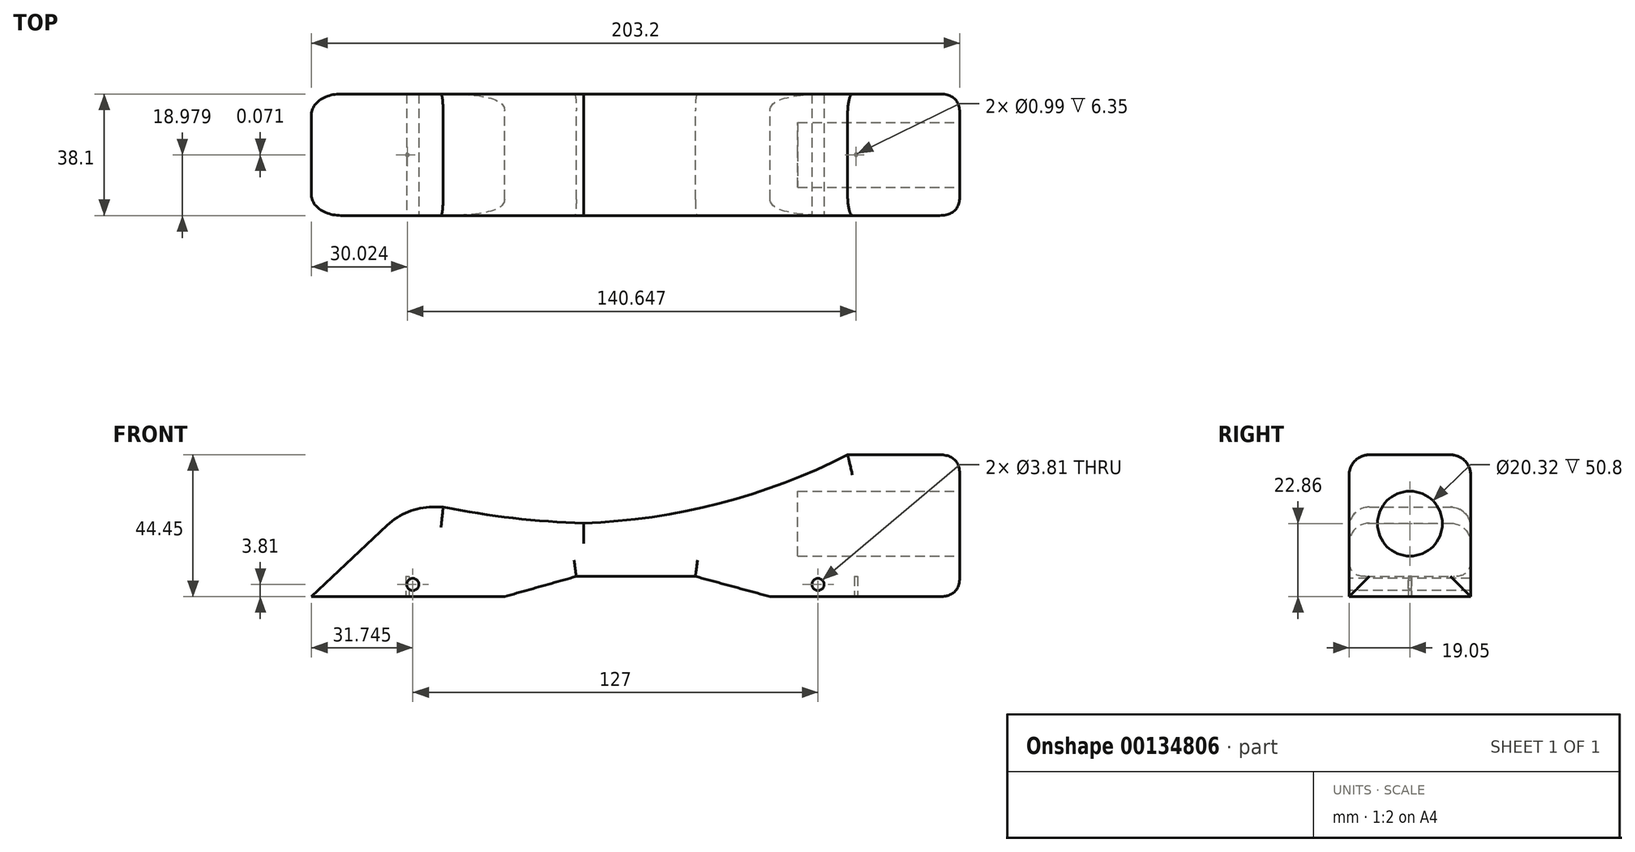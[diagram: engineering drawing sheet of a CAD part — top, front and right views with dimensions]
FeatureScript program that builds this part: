
annotation { "Feature Type Name" : "Feature", "Feature Type Description" : "" }
export const myFeature = defineFeature(function(context is Context, id is Id, definition is map)
    precondition{}
    {
        {
            var Q0;
            Q0=qCreatedBy(makeId("Front.planeOp"),FACE);
            var sketch = newSketch(context, id + "F0", { "sketchPlane" : qUnion([Q0])});
            skLineSegment(sketch, "E0", {"start": v(-93.71, 0) * mm, "end": v(-64, 28.05) * mm});
            skLineSegment(sketch, "E1", {"start": v(-64, 28.05) * mm, "end": v(-52.47, 28.05) * mm});
            skLineSegment(sketch, "E2", {"start": v(-52.47, 28.05) * mm, "end": v(-40.94, 22.9) * mm});
            skLineSegment(sketch, "E3", {"start": v(-40.94, 22.9) * mm, "end": v(49.74, 22.9) * mm});
            skLineSegment(sketch, "E4", {"start": v(49.74, 22.9) * mm, "end": v(74.3, 44.45) * mm});
            skLineSegment(sketch, "E5", {"start": v(74.3, 44.45) * mm, "end": v(109.49, 44.45) * mm});
            skLineSegment(sketch, "E6", {"start": v(109.49, 44.45) * mm, "end": v(109.49, 0) * mm});
            skLineSegment(sketch, "E7", {"start": v(109.49, 0) * mm, "end": v(-93.71, 0) * mm});
            skLineSegment(sketch, "E8", {"start": v(-33.22, 0) * mm, "end": v(-10.73, 6.32) * mm});
            skLineSegment(sketch, "E9", {"start": v(-10.73, 6.32) * mm, "end": v(26.6, 6.32) * mm});
            skLineSegment(sketch, "E10", {"start": v(26.6, 6.32) * mm, "end": v(50.03, 0) * mm});
            skSolve(sketch);
        }
        {
            var Q0;
            Q0=makeQuery(id+"F0.imprint","IMPRINT",FACE,{"disambiguationData":[TD([[makeQuery(id+"F0.imprint","IMPRINT",EDGE,{"derivedFrom":sQuery(id+"F0.wireOp",EDGE,"E0")}),-1.0]])]});
            extrude(context, id + "F1", {"entities" : qUnion([Q0]), "depth" : 38.1 * mm});
        }
        {
            var Q0;
            Q0=makeQuery(id+"F1.opExtrude","SWEPT_EDGE",EDGE,{"disambiguationData":[OSD([sQuery(id+"F0.wireOp",EDGE,"E0"),sQuery(id+"F0.wireOp",EDGE,"E1")])]});
            fillet(context, id + "F2", {"entities" : qUnion([Q0]), "radius" : 20.77 * mm, "tangentPropagation" : true, "allowEdgeOverflow" : false});
        }
        {
            var Q0;
            Q0=makeQuery(id+"F1.opExtrude","SWEPT_EDGE",EDGE,{"disambiguationData":[OSD([sQuery(id+"F0.wireOp",EDGE,"E3"),sQuery(id+"F0.wireOp",EDGE,"E4")])]});
            fillet(context, id + "F3", {"entities" : qUnion([Q0]), "radius" : 197.48 * mm, "tangentPropagation" : true, "allowEdgeOverflow" : false});
        }
        {
            var Q0;
            Q0=makeQuery(id+"F1.opExtrude","SWEPT_EDGE",EDGE,{"disambiguationData":[OSD([sQuery(id+"F0.wireOp",EDGE,"E2"),sQuery(id+"F0.wireOp",EDGE,"E3")])]});
            fillet(context, id + "F4", {"entities" : qUnion([Q0]), "radius" : 266.42 * mm, "tangentPropagation" : true, "allowEdgeOverflow" : false});
        }
        {
            var Q0;
            Q0=makeQuery(id+"F1.opExtrude","CAP_EDGE",EDGE,{"disambiguationData":[OSD([sQuery(id+"F0.wireOp",EDGE,"E0")])],"isStart":false});
            var Q1;
            {var subQ0=sQuery(id+"F0.wireOp",EDGE,"E1");var subQ1=sQuery(id+"F0.wireOp",EDGE,"E0");Q1=makeQuery(id+"F2.opFillet","BLEND_EDGE",EDGE,{"blendedFrom":[makeQuery(id+"F1.opExtrude","SWEPT_EDGE",EDGE,{"disambiguationData":[OSD([subQ1,subQ0])]}),makeQuery(id+"F1.opExtrude","CAP_FACE",FACE,{"disambiguationData":[OSD([subQ1,subQ0,sQuery(id+"F0.wireOp",EDGE,"E2"),sQuery(id+"F0.wireOp",EDGE,"E3"),sQuery(id+"F0.wireOp",EDGE,"E4"),sQuery(id+"F0.wireOp",EDGE,"E5"),sQuery(id+"F0.wireOp",EDGE,"E6"),sQuery(id+"F0.wireOp",EDGE,"E7")])],"isStart":false})],"blendedInto":[makeQuery(id+"F1.opExtrude","CAP_FACE",FACE,{"disambiguationData":[OSD([subQ1,subQ0,sQuery(id+"F0.wireOp",EDGE,"E2"),sQuery(id+"F0.wireOp",EDGE,"E3"),sQuery(id+"F0.wireOp",EDGE,"E4"),sQuery(id+"F0.wireOp",EDGE,"E5"),sQuery(id+"F0.wireOp",EDGE,"E6"),sQuery(id+"F0.wireOp",EDGE,"E7")])],"isStart":false})]});}
            var Q2;
            {var subQ0=sQuery(id+"F0.wireOp",EDGE,"E3");var subQ1=sQuery(id+"F0.wireOp",EDGE,"E2");Q2=makeQuery(id+"F4.opFillet","BLEND_EDGE",EDGE,{"blendedFrom":[makeQuery(id+"F1.opExtrude","SWEPT_EDGE",EDGE,{"disambiguationData":[OSD([subQ1,subQ0])]}),makeQuery(id+"F1.opExtrude","CAP_FACE",FACE,{"disambiguationData":[OSD([sQuery(id+"F0.wireOp",EDGE,"E0"),sQuery(id+"F0.wireOp",EDGE,"E1"),subQ1,subQ0,sQuery(id+"F0.wireOp",EDGE,"E4"),sQuery(id+"F0.wireOp",EDGE,"E5"),sQuery(id+"F0.wireOp",EDGE,"E6"),sQuery(id+"F0.wireOp",EDGE,"E7")])],"isStart":false})],"blendedInto":[makeQuery(id+"F1.opExtrude","CAP_FACE",FACE,{"disambiguationData":[OSD([sQuery(id+"F0.wireOp",EDGE,"E0"),sQuery(id+"F0.wireOp",EDGE,"E1"),subQ1,subQ0,sQuery(id+"F0.wireOp",EDGE,"E4"),sQuery(id+"F0.wireOp",EDGE,"E5"),sQuery(id+"F0.wireOp",EDGE,"E6"),sQuery(id+"F0.wireOp",EDGE,"E7")])],"isStart":false})]});}
            var Q3;
            {var subQ0=sQuery(id+"F0.wireOp",EDGE,"E4");var subQ1=sQuery(id+"F0.wireOp",EDGE,"E3");Q3=makeQuery(id+"F3.opFillet","BLEND_EDGE",EDGE,{"blendedFrom":[makeQuery(id+"F1.opExtrude","SWEPT_EDGE",EDGE,{"disambiguationData":[OSD([subQ1,subQ0])]}),makeQuery(id+"F1.opExtrude","CAP_FACE",FACE,{"disambiguationData":[OSD([sQuery(id+"F0.wireOp",EDGE,"E0"),sQuery(id+"F0.wireOp",EDGE,"E1"),sQuery(id+"F0.wireOp",EDGE,"E2"),subQ1,subQ0,sQuery(id+"F0.wireOp",EDGE,"E5"),sQuery(id+"F0.wireOp",EDGE,"E6"),sQuery(id+"F0.wireOp",EDGE,"E7")])],"isStart":false})],"blendedInto":[makeQuery(id+"F1.opExtrude","CAP_FACE",FACE,{"disambiguationData":[OSD([sQuery(id+"F0.wireOp",EDGE,"E0"),sQuery(id+"F0.wireOp",EDGE,"E1"),sQuery(id+"F0.wireOp",EDGE,"E2"),subQ1,subQ0,sQuery(id+"F0.wireOp",EDGE,"E5"),sQuery(id+"F0.wireOp",EDGE,"E6"),sQuery(id+"F0.wireOp",EDGE,"E7")])],"isStart":false})]});}
            var Q4;
            Q4=makeQuery(id+"F1.opExtrude","CAP_EDGE",EDGE,{"disambiguationData":[OSD([sQuery(id+"F0.wireOp",EDGE,"E5")])],"isStart":false});
            fillet(context, id + "F5", {"entities" : qUnion([Q0, Q1, Q2, Q3, Q4]), "radius" : 6.35 * mm, "tangentPropagation" : true, "allowEdgeOverflow" : false});
        }
        {
            var Q0;
            Q0=makeQuery(id+"F1.opExtrude","CAP_EDGE",EDGE,{"disambiguationData":[OSD([sQuery(id+"F0.wireOp",EDGE,"E0")])],"isStart":true});
            var Q1;
            {var subQ0=sQuery(id+"F0.wireOp",EDGE,"E1");var subQ1=sQuery(id+"F0.wireOp",EDGE,"E0");Q1=makeQuery(id+"F2.opFillet","BLEND_EDGE",EDGE,{"blendedFrom":[makeQuery(id+"F1.opExtrude","SWEPT_EDGE",EDGE,{"disambiguationData":[OSD([subQ1,subQ0])]}),makeQuery(id+"F1.opExtrude","CAP_FACE",FACE,{"disambiguationData":[OSD([subQ1,subQ0,sQuery(id+"F0.wireOp",EDGE,"E2"),sQuery(id+"F0.wireOp",EDGE,"E3"),sQuery(id+"F0.wireOp",EDGE,"E4"),sQuery(id+"F0.wireOp",EDGE,"E5"),sQuery(id+"F0.wireOp",EDGE,"E6"),sQuery(id+"F0.wireOp",EDGE,"E7")])],"isStart":true})],"blendedInto":[makeQuery(id+"F1.opExtrude","CAP_FACE",FACE,{"disambiguationData":[OSD([subQ1,subQ0,sQuery(id+"F0.wireOp",EDGE,"E2"),sQuery(id+"F0.wireOp",EDGE,"E3"),sQuery(id+"F0.wireOp",EDGE,"E4"),sQuery(id+"F0.wireOp",EDGE,"E5"),sQuery(id+"F0.wireOp",EDGE,"E6"),sQuery(id+"F0.wireOp",EDGE,"E7")])],"isStart":true})]});}
            var Q2;
            {var subQ0=sQuery(id+"F0.wireOp",EDGE,"E3");var subQ1=sQuery(id+"F0.wireOp",EDGE,"E2");Q2=makeQuery(id+"F4.opFillet","BLEND_EDGE",EDGE,{"blendedFrom":[makeQuery(id+"F1.opExtrude","SWEPT_EDGE",EDGE,{"disambiguationData":[OSD([subQ1,subQ0])]}),makeQuery(id+"F1.opExtrude","CAP_FACE",FACE,{"disambiguationData":[OSD([sQuery(id+"F0.wireOp",EDGE,"E0"),sQuery(id+"F0.wireOp",EDGE,"E1"),subQ1,subQ0,sQuery(id+"F0.wireOp",EDGE,"E4"),sQuery(id+"F0.wireOp",EDGE,"E5"),sQuery(id+"F0.wireOp",EDGE,"E6"),sQuery(id+"F0.wireOp",EDGE,"E7")])],"isStart":true})],"blendedInto":[makeQuery(id+"F1.opExtrude","CAP_FACE",FACE,{"disambiguationData":[OSD([sQuery(id+"F0.wireOp",EDGE,"E0"),sQuery(id+"F0.wireOp",EDGE,"E1"),subQ1,subQ0,sQuery(id+"F0.wireOp",EDGE,"E4"),sQuery(id+"F0.wireOp",EDGE,"E5"),sQuery(id+"F0.wireOp",EDGE,"E6"),sQuery(id+"F0.wireOp",EDGE,"E7")])],"isStart":true})]});}
            var Q3;
            {var subQ0=sQuery(id+"F0.wireOp",EDGE,"E4");var subQ1=sQuery(id+"F0.wireOp",EDGE,"E3");Q3=makeQuery(id+"F3.opFillet","BLEND_EDGE",EDGE,{"blendedFrom":[makeQuery(id+"F1.opExtrude","SWEPT_EDGE",EDGE,{"disambiguationData":[OSD([subQ1,subQ0])]}),makeQuery(id+"F1.opExtrude","CAP_FACE",FACE,{"disambiguationData":[OSD([sQuery(id+"F0.wireOp",EDGE,"E0"),sQuery(id+"F0.wireOp",EDGE,"E1"),sQuery(id+"F0.wireOp",EDGE,"E2"),subQ1,subQ0,sQuery(id+"F0.wireOp",EDGE,"E5"),sQuery(id+"F0.wireOp",EDGE,"E6"),sQuery(id+"F0.wireOp",EDGE,"E7")])],"isStart":true})],"blendedInto":[makeQuery(id+"F1.opExtrude","CAP_FACE",FACE,{"disambiguationData":[OSD([sQuery(id+"F0.wireOp",EDGE,"E0"),sQuery(id+"F0.wireOp",EDGE,"E1"),sQuery(id+"F0.wireOp",EDGE,"E2"),subQ1,subQ0,sQuery(id+"F0.wireOp",EDGE,"E5"),sQuery(id+"F0.wireOp",EDGE,"E6"),sQuery(id+"F0.wireOp",EDGE,"E7")])],"isStart":true})]});}
            var Q4;
            Q4=makeQuery(id+"F1.opExtrude","CAP_EDGE",EDGE,{"disambiguationData":[OSD([sQuery(id+"F0.wireOp",EDGE,"E5")])],"isStart":true});
            fillet(context, id + "F6", {"entities" : qUnion([Q0, Q1, Q2, Q3, Q4]), "radius" : 6.35 * mm, "tangentPropagation" : true, "allowEdgeOverflow" : false});
        }
        {
            var Q0;
            Q0=makeQuery(id+"F1.opExtrude","CAP_FACE",FACE,{"disambiguationData":[OSD([sQuery(id+"F0.wireOp",EDGE,"E0"),sQuery(id+"F0.wireOp",EDGE,"E1"),sQuery(id+"F0.wireOp",EDGE,"E2"),sQuery(id+"F0.wireOp",EDGE,"E3"),sQuery(id+"F0.wireOp",EDGE,"E4"),sQuery(id+"F0.wireOp",EDGE,"E5"),sQuery(id+"F0.wireOp",EDGE,"E6"),sQuery(id+"F0.wireOp",EDGE,"E7"),sQuery(id+"F0.wireOp",EDGE,"E8"),sQuery(id+"F0.wireOp",EDGE,"E9"),sQuery(id+"F0.wireOp",EDGE,"E10")])],"isStart":false});
            var sketch = newSketch(context, id + "F7", { "sketchPlane" : qUnion([Q0])});
            skCircle(sketch, "E11", {"center": v(-61.96, 3.81) * mm, "radius": 1.9 * mm});
            skSolve(sketch);
        }
        {
            var Q0;
            Q0=makeQuery(id+"F7.imprint","IMPRINT",FACE,{"disambiguationData":[TD([[makeQuery(id+"F7.imprint","IMPRINT",EDGE,{"derivedFrom":sQuery(id+"F7.wireOp",EDGE,"E11")}),1.0]])]});
            extrude(context, id + "F8", {"entities" : qUnion([Q0]), "operationType" : NewBodyOperationType.REMOVE, "endBound" : BoundingType.THROUGH_ALL, "oppositeDirection" : true, "depth" : 25.4 * mm});
        }
        {
            var Q0;
            Q0=makeQuery(id+"F1.opExtrude","CAP_FACE",FACE,{"disambiguationData":[OSD([sQuery(id+"F0.wireOp",EDGE,"E0"),sQuery(id+"F0.wireOp",EDGE,"E1"),sQuery(id+"F0.wireOp",EDGE,"E2"),sQuery(id+"F0.wireOp",EDGE,"E3"),sQuery(id+"F0.wireOp",EDGE,"E4"),sQuery(id+"F0.wireOp",EDGE,"E5"),sQuery(id+"F0.wireOp",EDGE,"E6"),sQuery(id+"F0.wireOp",EDGE,"E7"),sQuery(id+"F0.wireOp",EDGE,"E8"),sQuery(id+"F0.wireOp",EDGE,"E9"),sQuery(id+"F0.wireOp",EDGE,"E10")])],"isStart":false});
            var sketch = newSketch(context, id + "F9", { "sketchPlane" : qUnion([Q0])});
            skCircle(sketch, "E12", {"center": v(65.04, 3.81) * mm, "radius": 1.9 * mm});
            skSolve(sketch);
        }
        {
            var Q0;
            Q0=makeQuery(id+"F9.imprint","IMPRINT",FACE,{"disambiguationData":[TD([[makeQuery(id+"F9.imprint","IMPRINT",EDGE,{"derivedFrom":sQuery(id+"F9.wireOp",EDGE,"E12")}),1.0]])]});
            var Q1;
            Q1=sQuery(id+"F9.wireOp",EDGE,"E12");
            extrude(context, id + "F10", {"entities" : qUnion([Q0]), "operationType" : NewBodyOperationType.REMOVE, "surfaceEntities" : qUnion([Q1]), "endBound" : BoundingType.THROUGH_ALL, "oppositeDirection" : true, "depth" : 25.4 * mm});
        }
        {
            var Q0;
            Q0=makeQuery(id+"F1.opExtrude","SWEPT_FACE",FACE,{"disambiguationData":[OSD([sQuery(id+"F0.wireOp",EDGE,"E6")])]});
            var sketch = newSketch(context, id + "F11", { "sketchPlane" : qUnion([Q0])});
            skCircle(sketch, "E13", {"center": v(-19.05, 22.86) * mm, "radius": 10.16 * mm});
            skSolve(sketch);
        }
        {
            var Q0;
            Q0=makeQuery(id+"F11.imprint","IMPRINT",FACE,{"disambiguationData":[TD([[makeQuery(id+"F11.imprint","IMPRINT",EDGE,{"derivedFrom":sQuery(id+"F11.wireOp",EDGE,"E13")}),1.0]])]});
            var Q1;
            Q1=sQuery(id+"F11.wireOp",EDGE,"E13");
            extrude(context, id + "F12", {"entities" : qUnion([Q0]), "operationType" : NewBodyOperationType.REMOVE, "surfaceEntities" : qUnion([Q1]), "oppositeDirection" : true, "depth" : 50.8 * mm});
        }
        {
            var Q0;
            Q0=makeQuery(id+"F1.opExtrude","CAP_EDGE",EDGE,{"disambiguationData":[OSD([sQuery(id+"F0.wireOp",EDGE,"E8")])],"isStart":false});
            var Q1;
            Q1=makeQuery(id+"F1.opExtrude","CAP_EDGE",EDGE,{"disambiguationData":[OSD([sQuery(id+"F0.wireOp",EDGE,"E9")])],"isStart":false});
            var Q2;
            Q2=makeQuery(id+"F1.opExtrude","CAP_EDGE",EDGE,{"disambiguationData":[OSD([sQuery(id+"F0.wireOp",EDGE,"E10")])],"isStart":false});
            fillet(context, id + "F13", {"entities" : qUnion([Q0, Q1, Q2]), "radius" : 5.08 * mm, "tangentPropagation" : true, "rho" : 0.5, "crossSection" : FilletCrossSection.CONIC, "allowEdgeOverflow" : false});
        }
        {
            var Q0;
            Q0=makeQuery(id+"F1.opExtrude","CAP_EDGE",EDGE,{"disambiguationData":[OSD([sQuery(id+"F0.wireOp",EDGE,"E10")])],"isStart":true});
            var Q1;
            Q1=makeQuery(id+"F1.opExtrude","CAP_EDGE",EDGE,{"disambiguationData":[OSD([sQuery(id+"F0.wireOp",EDGE,"E9")])],"isStart":true});
            var Q2;
            Q2=makeQuery(id+"F1.opExtrude","CAP_EDGE",EDGE,{"disambiguationData":[OSD([sQuery(id+"F0.wireOp",EDGE,"E8")])],"isStart":true});
            fillet(context, id + "F14", {"entities" : qUnion([Q0, Q1, Q2]), "radius" : 5.08 * mm, "tangentPropagation" : true, "rho" : 0.5, "crossSection" : FilletCrossSection.CONIC, "allowEdgeOverflow" : false});
        }
        {
            var Q0;
            Q0=makeQuery(id+"F1.opExtrude","CAP_EDGE",EDGE,{"disambiguationData":[OSD([sQuery(id+"F0.wireOp",EDGE,"E6")])],"isStart":false});
            var Q1;
            Q1=makeQuery(id+"F1.opExtrude","SWEPT_EDGE",EDGE,{"disambiguationData":[OSD([sQuery(id+"F0.wireOp",EDGE,"E6"),sQuery(id+"F0.wireOp",EDGE,"E7")])]});
            var Q2;
            Q2=makeQuery(id+"F1.opExtrude","CAP_EDGE",EDGE,{"disambiguationData":[OSD([sQuery(id+"F0.wireOp",EDGE,"E6")])],"isStart":true});
            fillet(context, id + "F15", {"entities" : qUnion([Q0, Q1, Q2]), "radius" : 6.35 * mm, "tangentPropagation" : true, "rho" : 0.5, "crossSection" : FilletCrossSection.CONIC, "allowEdgeOverflow" : false});
        }
        {
            var Q0;
            {var subQ0=sQuery(id+"F0.wireOp",EDGE,"E7");Q0=makeQuery(id+"F1.opExtrude","SWEPT_FACE",FACE,{"disambiguationData":[OSD([subQ0]),TDD([makeQuery(id+"F0.imprint","IMPRINT",EDGE,{"disambiguationData":[TD([[makeQuery(id+"F0.imprint","INTERSECT",VERTEX,{"derivedFrom":[sQuery(id+"F0.wireOp",EDGE,"E0"),subQ0]}),1.0]])],"derivedFrom":subQ0})])]});}
            var sketch = newSketch(context, id + "F16", { "sketchPlane" : qUnion([Q0])});
            skCircle(sketch, "E14", {"center": v(-63.69, 19.12) * mm, "radius": 0.5 * mm});
            skSolve(sketch);
        }
        {
            var Q0;
            Q0=makeQuery(id+"F16.imprint","IMPRINT",FACE,{"disambiguationData":[TD([[makeQuery(id+"F16.imprint","IMPRINT",EDGE,{"derivedFrom":sQuery(id+"F16.wireOp",EDGE,"E14")}),1.0]])]});
            extrude(context, id + "F17", {"entities" : qUnion([Q0]), "operationType" : NewBodyOperationType.REMOVE, "oppositeDirection" : true, "depth" : 6.35 * mm});
        }
        {
            var Q0;
            {var subQ0=sQuery(id+"F0.wireOp",EDGE,"E7");Q0=makeQuery(id+"F1.opExtrude","SWEPT_FACE",FACE,{"disambiguationData":[OSD([subQ0]),TDD([makeQuery(id+"F0.imprint","IMPRINT",EDGE,{"disambiguationData":[TD([[makeQuery(id+"F0.imprint","INTERSECT",VERTEX,{"derivedFrom":[sQuery(id+"F0.wireOp",EDGE,"E6"),subQ0]}),-1.0]])],"derivedFrom":subQ0})])]});}
            var sketch = newSketch(context, id + "F18", { "sketchPlane" : qUnion([Q0])});
            skCircle(sketch, "E15", {"center": v(76.96, 19.05) * mm, "radius": 0.5 * mm});
            skSolve(sketch);
        }
        {
            var Q0;
            Q0=makeQuery(id+"F18.imprint","IMPRINT",FACE,{"disambiguationData":[TD([[makeQuery(id+"F18.imprint","IMPRINT",EDGE,{"derivedFrom":sQuery(id+"F18.wireOp",EDGE,"E15")}),1.0]])]});
            extrude(context, id + "F19", {"entities" : qUnion([Q0]), "operationType" : NewBodyOperationType.REMOVE, "oppositeDirection" : true, "depth" : 6.35 * mm});
        }
    });
